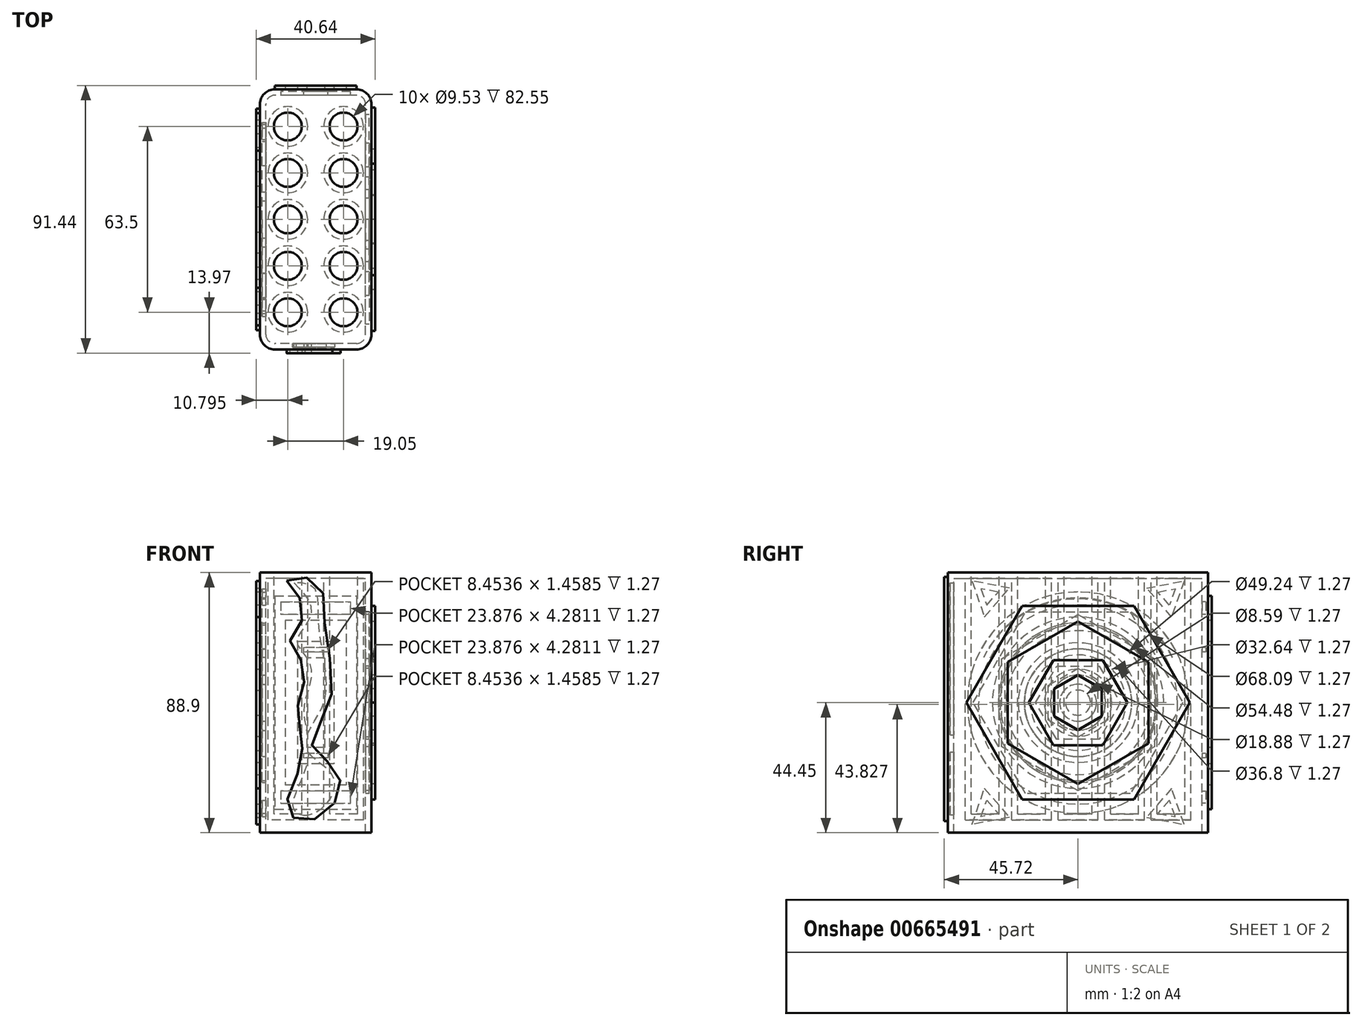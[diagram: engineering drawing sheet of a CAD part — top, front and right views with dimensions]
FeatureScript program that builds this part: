
annotation { "Feature Type Name" : "Feature", "Feature Type Description" : "" }
export const myFeature = defineFeature(function(context is Context, id is Id, definition is map)
    precondition{}
    {
        {
            var Q0;
            Q0=qCreatedBy(makeId("Right.planeOp"),FACE);
            var sketch = newSketch(context, id + "F0", { "sketchPlane" : qUnion([Q0])});
            skLineSegment(sketch, "E0.bottom", {"start": v(-44.45, 44.45) * mm, "end": v(44.45, 44.45) * mm});
            skLineSegment(sketch, "E0.top", {"start": v(-44.45, -44.45) * mm, "end": v(44.45, -44.45) * mm});
            skLineSegment(sketch, "E0.left", {"start": v(-44.45, 44.45) * mm, "end": v(-44.45, -44.45) * mm});
            skLineSegment(sketch, "E0.right", {"start": v(44.45, 44.45) * mm, "end": v(44.45, -44.45) * mm});
            skPoint(sketch, "E0.middle", {"position": v(0, 0) * mm});
            skSolve(sketch);
        }
        {
            var Q0;
            Q0=qSketchRegion(id+"F0",true);
            extrude(context, id + "F1", {"entities" : qUnion([Q0]), "endBound" : BoundingType.SYMMETRIC, "depth" : 38.1 * mm, "offsetDistance" : 25.4 * mm});
        }
        {
            var Q0;
            Q0=makeQuery(id+"F1.opExtrude","SWEPT_FACE",FACE,{"disambiguationData":[OSD([sQuery(id+"F0.wireOp",EDGE,"E0.bottom")])]});
            var sketch = newSketch(context, id + "F2", { "sketchPlane" : qUnion([Q0])});
            skCircle(sketch, "E1", {"center": v(-9.52, -31.75) * mm, "radius": 4.76 * mm});
            skCircle(sketch, "E2", {"center": v(-9.52, 0) * mm, "radius": 4.76 * mm});
            skCircle(sketch, "E3", {"center": v(-9.52, -15.88) * mm, "radius": 4.76 * mm});
            skCircle(sketch, "E4", {"center": v(-9.52, 15.88) * mm, "radius": 4.76 * mm});
            skCircle(sketch, "E5", {"center": v(-9.52, 31.75) * mm, "radius": 4.76 * mm});
            skCircle(sketch, "E6.MirrorC", {"center": v(9.52, 0) * mm, "radius": 4.76 * mm});
            skCircle(sketch, "E7.MirrorC", {"center": v(9.52, -31.75) * mm, "radius": 4.76 * mm});
            skCircle(sketch, "E8.MirrorC", {"center": v(9.52, -15.88) * mm, "radius": 4.76 * mm});
            skCircle(sketch, "E9.MirrorC", {"center": v(9.52, 15.88) * mm, "radius": 4.76 * mm});
            skCircle(sketch, "E10.MirrorC", {"center": v(9.52, 31.75) * mm, "radius": 4.76 * mm});
            skSolve(sketch);
        }
        {
            var Q0;
            Q0=qSketchRegion(id+"F2",true);
            extrude(context, id + "F3", {"entities" : qUnion([Q0]), "operationType" : NewBodyOperationType.REMOVE, "oppositeDirection" : true, "depth" : 82.55 * mm, "offsetDistance" : 25.4 * mm});
        }
        {
            var Q0;
            Q0=makeQuery(id+"F1.opExtrude","CAP_EDGE",EDGE,{"disambiguationData":[OSD([sQuery(id+"F0.wireOp",EDGE,"E0.left")])],"isStart":false});
            var Q1;
            Q1=makeQuery(id+"F1.opExtrude","CAP_EDGE",EDGE,{"disambiguationData":[OSD([sQuery(id+"F0.wireOp",EDGE,"E0.right")])],"isStart":false});
            var Q2;
            Q2=makeQuery(id+"F1.opExtrude","CAP_EDGE",EDGE,{"disambiguationData":[OSD([sQuery(id+"F0.wireOp",EDGE,"E0.right")])],"isStart":true});
            var Q3;
            Q3=makeQuery(id+"F1.opExtrude","CAP_EDGE",EDGE,{"disambiguationData":[OSD([sQuery(id+"F0.wireOp",EDGE,"E0.left")])],"isStart":true});
            fillet(context, id + "F4", {"entities" : qUnion([Q0, Q1, Q2, Q3]), "radius" : 5.08 * mm, "tangentPropagation" : true, "allowEdgeOverflow" : false});
        }
        {
            var Q0;
            Q0=makeQuery(id+"F1.opExtrude","CAP_FACE",FACE,{"disambiguationData":[OSD([sQuery(id+"F0.wireOp",EDGE,"E0.bottom"),sQuery(id+"F0.wireOp",EDGE,"E0.top"),sQuery(id+"F0.wireOp",EDGE,"E0.left"),sQuery(id+"F0.wireOp",EDGE,"E0.right")])],"isStart":false});
            var sketch = newSketch(context, id + "F5", { "sketchPlane" : qUnion([Q0])});
            skCircle(sketch, "E11.cCircle", {"center": v(0, 0) * mm, "radius": 8.15 * mm, "construction": true});
            skLineSegment(sketch, "E11.0", {"start": v(-8.15, -4.7) * mm, "end": v(-8.15, 4.7) * mm});
            skLineSegment(sketch, "E11.1", {"start": v(-8.15, 4.7) * mm, "end": v(0, 9.4) * mm});
            skLineSegment(sketch, "E11.2", {"start": v(0, 9.4) * mm, "end": v(8.15, 4.7) * mm});
            skLineSegment(sketch, "E11.3", {"start": v(8.15, 4.7) * mm, "end": v(8.15, -4.7) * mm});
            skLineSegment(sketch, "E11.4", {"start": v(8.15, -4.7) * mm, "end": v(0, -9.4) * mm});
            skLineSegment(sketch, "E11.5", {"start": v(0, -9.4) * mm, "end": v(-8.15, -4.7) * mm});
            skPoint(sketch, "E11.0.midPoint", {"position": v(-8.15, 0) * mm});
            skCircle(sketch, "E12.cCircle", {"center": v(0, 0) * mm, "radius": 14.58 * mm, "construction": true});
            skLineSegment(sketch, "E12.0", {"start": v(8.42, -14.58) * mm, "end": v(-8.42, -14.58) * mm});
            skLineSegment(sketch, "E12.1", {"start": v(-8.42, -14.58) * mm, "end": v(-16.84, 0) * mm});
            skLineSegment(sketch, "E12.2", {"start": v(-16.84, 0) * mm, "end": v(-8.42, 14.58) * mm});
            skLineSegment(sketch, "E12.3", {"start": v(-8.42, 14.58) * mm, "end": v(8.42, 14.58) * mm});
            skLineSegment(sketch, "E12.4", {"start": v(8.42, 14.58) * mm, "end": v(16.84, 0) * mm});
            skLineSegment(sketch, "E12.5", {"start": v(16.84, 0) * mm, "end": v(8.42, -14.58) * mm});
            skPoint(sketch, "E12.0.midPoint", {"position": v(0, -14.58) * mm});
            skCircle(sketch, "E13.cCircle", {"center": v(0, 0) * mm, "radius": 24.04 * mm, "construction": true});
            skLineSegment(sketch, "E13.0", {"start": v(-24.04, -13.88) * mm, "end": v(-24.04, 13.88) * mm});
            skLineSegment(sketch, "E13.1", {"start": v(-24.04, 13.88) * mm, "end": v(0, 27.76) * mm});
            skLineSegment(sketch, "E13.2", {"start": v(0, 27.76) * mm, "end": v(24.04, 13.88) * mm});
            skLineSegment(sketch, "E13.3", {"start": v(24.04, 13.88) * mm, "end": v(24.04, -13.88) * mm});
            skLineSegment(sketch, "E13.4", {"start": v(24.04, -13.88) * mm, "end": v(0, -27.76) * mm});
            skLineSegment(sketch, "E13.5", {"start": v(0, -27.76) * mm, "end": v(-24.04, -13.88) * mm});
            skPoint(sketch, "E13.0.midPoint", {"position": v(-24.04, 0) * mm});
            skCircle(sketch, "E14.cCircle", {"center": v(0, 0) * mm, "radius": 33.06 * mm, "construction": true});
            skLineSegment(sketch, "E14.0", {"start": v(19.08, -33.06) * mm, "end": v(-19.08, -33.06) * mm});
            skLineSegment(sketch, "E14.1", {"start": v(-19.08, -33.06) * mm, "end": v(-38.17, 0) * mm});
            skLineSegment(sketch, "E14.2", {"start": v(-38.17, 0) * mm, "end": v(-19.08, 33.06) * mm});
            skLineSegment(sketch, "E14.3", {"start": v(-19.08, 33.06) * mm, "end": v(19.08, 33.06) * mm});
            skLineSegment(sketch, "E14.4", {"start": v(19.08, 33.06) * mm, "end": v(38.17, 0) * mm});
            skLineSegment(sketch, "E14.5", {"start": v(38.17, 0) * mm, "end": v(19.08, -33.06) * mm});
            skPoint(sketch, "E14.0.midPoint", {"position": v(0, -33.06) * mm});
            skSolve(sketch);
        }
        {
            var Q0;
            Q0=makeQuery(id+"F5.imprint","IMPRINT",FACE,{"disambiguationData":[TD([[makeQuery(id+"F5.imprint","IMPRINT",EDGE,{"derivedFrom":sQuery(id+"F5.wireOp",EDGE,"E11.0")}),1.0]])]});
            var Q1;
            Q1=makeQuery(id+"F5.imprint","IMPRINT",FACE,{"disambiguationData":[TD([[makeQuery(id+"F5.imprint","IMPRINT",EDGE,{"derivedFrom":sQuery(id+"F5.wireOp",EDGE,"E13.0")}),1.0]])]});
            extrude(context, id + "F6", {"entities" : qUnion([Q0, Q1]), "operationType" : NewBodyOperationType.ADD, "depth" : 1.27 * mm, "offsetDistance" : 25.4 * mm});
        }
        {
            var Q0;
            Q0=makeQuery(id+"F1.opExtrude","CAP_FACE",FACE,{"disambiguationData":[OSD([sQuery(id+"F0.wireOp",EDGE,"E0.bottom"),sQuery(id+"F0.wireOp",EDGE,"E0.top"),sQuery(id+"F0.wireOp",EDGE,"E0.left"),sQuery(id+"F0.wireOp",EDGE,"E0.right")])],"isStart":true});
            var sketch = newSketch(context, id + "F7", { "sketchPlane" : qUnion([Q0])});
            skCircle(sketch, "E15", {"center": v(0, 0) * mm, "radius": 4.3 * mm});
            skCircle(sketch, "E16", {"center": v(0, 0) * mm, "radius": 11.47 * mm});
            skCircle(sketch, "E17", {"center": v(0, 0) * mm, "radius": 16.32 * mm});
            skCircle(sketch, "E18", {"center": v(0, 0) * mm, "radius": 20.43 * mm});
            skCircle(sketch, "E19", {"center": v(0, 0) * mm, "radius": 24.62 * mm});
            skCircle(sketch, "E20", {"center": v(0, 0) * mm, "radius": 29.27 * mm});
            skCircle(sketch, "E21", {"center": v(0, -0.62) * mm, "radius": 34.04 * mm});
            skCircle(sketch, "E22", {"center": v(0, 0) * mm, "radius": 37.84 * mm});
            skSolve(sketch);
        }
        {
            var Q0;
            Q0=makeQuery(id+"F7.imprint","IMPRINT",FACE,{"disambiguationData":[TD([[makeQuery(id+"F7.imprint","IMPRINT",EDGE,{"derivedFrom":sQuery(id+"F7.wireOp",EDGE,"E15")}),-1.0]])]});
            var Q1;
            Q1=makeQuery(id+"F7.imprint","IMPRINT",FACE,{"disambiguationData":[TD([[makeQuery(id+"F7.imprint","IMPRINT",EDGE,{"derivedFrom":sQuery(id+"F7.wireOp",EDGE,"E17")}),-1.0]])]});
            var Q2;
            Q2=makeQuery(id+"F7.imprint","IMPRINT",FACE,{"disambiguationData":[TD([[makeQuery(id+"F7.imprint","IMPRINT",EDGE,{"derivedFrom":sQuery(id+"F7.wireOp",EDGE,"E19")}),-1.0]])]});
            var Q3;
            Q3=makeQuery(id+"F7.imprint","IMPRINT",FACE,{"disambiguationData":[TD([[makeQuery(id+"F7.imprint","IMPRINT",EDGE,{"derivedFrom":sQuery(id+"F7.wireOp",EDGE,"E21")}),-1.0]])]});
            extrude(context, id + "F8", {"entities" : qUnion([Q0, Q1, Q2, Q3]), "operationType" : NewBodyOperationType.ADD, "depth" : 1.27 * mm, "offsetDistance" : 25.4 * mm});
        }
        {
            var Q0;
            {var subQ0=sQuery(id+"F0.wireOp",EDGE,"E0.right");var subQ1=sQuery(id+"F0.wireOp",EDGE,"E0.bottom");var subQ2=sQuery(id+"F0.wireOp",EDGE,"E0.top");var subQ3=sQuery(id+"F0.wireOp",EDGE,"E0.left");Q0=makeQuery(id+"F8.boolean.opBoolean","SPLIT",FACE,{"disambiguationData":[TD([makeQuery(id+"F1.opExtrude","SWEPT_FACE",FACE,{"disambiguationData":[OSD([subQ1])]})])],"derivedFrom":makeQuery(id+"F1.opExtrude","CAP_FACE",FACE,{"disambiguationData":[OSD([subQ1,subQ2,subQ3,subQ0])],"isStart":true})});}
            var sketch = newSketch(context, id + "F9", { "sketchPlane" : qUnion([Q0])});
            skCircle(sketch, "E23.cCircle", {"center": v(30.56, 36.7) * mm, "radius": 3.76 * mm, "construction": true});
            skLineSegment(sketch, "E23.0", {"start": v(36.24, 41.63) * mm, "end": v(32, 29.3) * mm});
            skLineSegment(sketch, "E23.1", {"start": v(32, 29.3) * mm, "end": v(23.44, 39.15) * mm});
            skLineSegment(sketch, "E23.2", {"start": v(23.44, 39.15) * mm, "end": v(36.24, 41.63) * mm});
            skPoint(sketch, "E23.0.midPoint", {"position": v(34.12, 35.47) * mm});
            skCircle(sketch, "E24.MirrorC", {"center": v(-30.56, 36.7) * mm, "radius": 3.76 * mm, "construction": true});
            skLineSegment(sketch, "E25.MirrorCS", {"start": v(-36.24, 41.63) * mm, "end": v(-32, 29.3) * mm});
            skLineSegment(sketch, "E26.MirrorCS", {"start": v(-23.44, 39.15) * mm, "end": v(-36.24, 41.63) * mm});
            skLineSegment(sketch, "E27.MirrorCS", {"start": v(-32, 29.3) * mm, "end": v(-23.44, 39.15) * mm});
            skPoint(sketch, "E28.MirrorP", {"position": v(-34.12, 35.47) * mm});
            skLineSegment(sketch, "E29.MirrorCS", {"start": v(-36.24, -41.63) * mm, "end": v(-32, -29.3) * mm});
            skCircle(sketch, "E30.MirrorC", {"center": v(-30.56, -36.7) * mm, "radius": 3.76 * mm, "construction": true});
            skLineSegment(sketch, "E31.MirrorCS", {"start": v(23.44, -39.15) * mm, "end": v(36.24, -41.63) * mm});
            skLineSegment(sketch, "E32.MirrorCS", {"start": v(-32, -29.3) * mm, "end": v(-23.44, -39.15) * mm});
            skLineSegment(sketch, "E33.MirrorCS", {"start": v(32, -29.3) * mm, "end": v(23.44, -39.15) * mm});
            skCircle(sketch, "E34.MirrorC", {"center": v(30.56, -36.7) * mm, "radius": 3.76 * mm, "construction": true});
            skLineSegment(sketch, "E35.MirrorCS", {"start": v(-23.44, -39.15) * mm, "end": v(-36.24, -41.63) * mm});
            skLineSegment(sketch, "E36.MirrorCS", {"start": v(36.24, -41.63) * mm, "end": v(32, -29.3) * mm});
            skPoint(sketch, "E37.MirrorP", {"position": v(34.12, -35.47) * mm});
            skPoint(sketch, "E38.MirrorP", {"position": v(-34.12, -35.47) * mm});
            skSolve(sketch);
        }
        {
            var Q0;
            Q0=makeQuery(id+"F9.imprint","IMPRINT",FACE,{"disambiguationData":[TD([[makeQuery(id+"F9.imprint","IMPRINT",EDGE,{"derivedFrom":sQuery(id+"F9.wireOp",EDGE,"E25.MirrorCS")}),1.0]])]});
            var Q1;
            Q1=makeQuery(id+"F9.imprint","IMPRINT",FACE,{"disambiguationData":[TD([[makeQuery(id+"F9.imprint","IMPRINT",EDGE,{"derivedFrom":sQuery(id+"F9.wireOp",EDGE,"E23.0")}),-1.0]])]});
            var Q2;
            Q2=makeQuery(id+"F9.imprint","IMPRINT",FACE,{"disambiguationData":[TD([[makeQuery(id+"F9.imprint","IMPRINT",EDGE,{"derivedFrom":sQuery(id+"F9.wireOp",EDGE,"E31.MirrorCS")}),1.0]])]});
            var Q3;
            Q3=makeQuery(id+"F9.imprint","IMPRINT",FACE,{"disambiguationData":[TD([[makeQuery(id+"F9.imprint","IMPRINT",EDGE,{"derivedFrom":sQuery(id+"F9.wireOp",EDGE,"E29.MirrorCS")}),-1.0]])]});
            extrude(context, id + "F10", {"entities" : qUnion([Q0, Q1, Q2, Q3]), "operationType" : NewBodyOperationType.ADD, "depth" : 1.27 * mm, "offsetDistance" : 25.4 * mm});
        }
        {
            var Q0;
            Q0=makeQuery(id+"F1.opExtrude","SWEPT_FACE",FACE,{"disambiguationData":[OSD([sQuery(id+"F0.wireOp",EDGE,"E0.right")])]});
            var sketch = newSketch(context, id + "F11", { "sketchPlane" : qUnion([Q0])});
            skLineSegment(sketch, "E39.bottom", {"start": v(13.97, -36.45) * mm, "end": v(-13.97, -36.45) * mm});
            skLineSegment(sketch, "E39.top", {"start": v(13.97, 36.45) * mm, "end": v(-13.97, 36.45) * mm});
            skLineSegment(sketch, "E39.left", {"start": v(13.97, -36.45) * mm, "end": v(13.97, 36.45) * mm});
            skLineSegment(sketch, "E39.right", {"start": v(-13.97, -36.45) * mm, "end": v(-13.97, 36.45) * mm});
            skPoint(sketch, "E39.middle", {"position": v(0, 0) * mm});
            skLineSegment(sketch, "E40.bottom", {"start": v(-10.43, 28.1) * mm, "end": v(10.43, 28.1) * mm});
            skLineSegment(sketch, "E40.top", {"start": v(-10.43, -28.1) * mm, "end": v(10.43, -28.1) * mm});
            skLineSegment(sketch, "E40.left", {"start": v(-10.43, 28.1) * mm, "end": v(-10.43, -28.1) * mm});
            skLineSegment(sketch, "E40.right", {"start": v(10.43, 28.1) * mm, "end": v(10.43, -28.1) * mm});
            skLineSegment(sketch, "E41.bottom", {"start": v(-6.26, 20.86) * mm, "end": v(6.26, 20.86) * mm});
            skLineSegment(sketch, "E41.top", {"start": v(-6.26, -20.86) * mm, "end": v(6.26, -20.86) * mm});
            skLineSegment(sketch, "E41.left", {"start": v(-6.26, 20.86) * mm, "end": v(-6.26, -20.86) * mm});
            skLineSegment(sketch, "E41.right", {"start": v(6.26, 20.86) * mm, "end": v(6.26, -20.86) * mm});
            skLineSegment(sketch, "E42.bottom", {"start": v(-3.07, 15.34) * mm, "end": v(3.07, 15.34) * mm});
            skLineSegment(sketch, "E42.top", {"start": v(-3.07, -15.34) * mm, "end": v(3.07, -15.34) * mm});
            skLineSegment(sketch, "E42.left", {"start": v(-3.07, 15.34) * mm, "end": v(-3.07, -15.34) * mm});
            skLineSegment(sketch, "E42.right", {"start": v(3.07, 15.34) * mm, "end": v(3.07, -15.34) * mm});
            skSolve(sketch);
        }
        {
            var Q0;
            Q0=makeQuery(id+"F11.imprint","IMPRINT",FACE,{"disambiguationData":[TD([[makeQuery(id+"F11.imprint","IMPRINT",EDGE,{"derivedFrom":sQuery(id+"F11.wireOp",EDGE,"E39.bottom")}),-1.0]])]});
            var Q1;
            Q1=makeQuery(id+"F11.imprint","IMPRINT",FACE,{"disambiguationData":[TD([[makeQuery(id+"F11.imprint","IMPRINT",EDGE,{"derivedFrom":sQuery(id+"F11.wireOp",EDGE,"E41.bottom")}),-1.0]])]});
            extrude(context, id + "F12", {"entities" : qUnion([Q0, Q1]), "operationType" : NewBodyOperationType.ADD, "depth" : 1.27 * mm, "offsetDistance" : 25.4 * mm});
        }
        {
            var Q0;
            Q0=makeQuery(id+"F1.opExtrude","SWEPT_FACE",FACE,{"disambiguationData":[OSD([sQuery(id+"F0.wireOp",EDGE,"E0.left")])]});
            var sketch = newSketch(context, id + "F13", { "sketchPlane" : qUnion([Q0])});
            skFitSpline(sketch, "E43", {"points": [v(-9.94, 41.73) * mm, v(-3.56, 32.28) * mm, v(-8.71, 21.35) * mm, v(-3.8, 12.15) * mm, v(-5.9, 0) * mm, v(-5.15, -9.7) * mm, v(-5.4, -21.84) * mm, v(-9.82, -35.83) * mm, v(-3.56, -40.5) * mm, v(7.12, -33.26) * mm, v(6.75, -22.7) * mm, v(-1.35, -14.48) * mm, v(4.9, 0) * mm, v(3.07, 27.12) * mm, v(0, 41.48) * mm, v(-9.94, 41.73) * mm]});
            skSolve(sketch);
        }
        {
            var Q0;
            Q0=makeQuery(id+"F13.imprint","IMPRINT",FACE,{"disambiguationData":[TD([[makeQuery(id+"F13.imprint","IMPRINT",EDGE,{"derivedFrom":sQuery(id+"F13.wireOp",EDGE,"E43")}),1.0]])]});
            extrude(context, id + "F14", {"entities" : qUnion([Q0]), "operationType" : NewBodyOperationType.ADD, "depth" : 1.27 * mm, "offsetDistance" : 25.4 * mm});
        }
        {
            var Q0;
            Q0=makeQuery(id+"F1.opExtrude","SWEPT_FACE",FACE,{"disambiguationData":[OSD([sQuery(id+"F0.wireOp",EDGE,"E0.top")])]});
            shell(context, id + "F15", {"entities" : qUnion([Q0]), "thickness" : 2.03 * mm});
        }
    });
